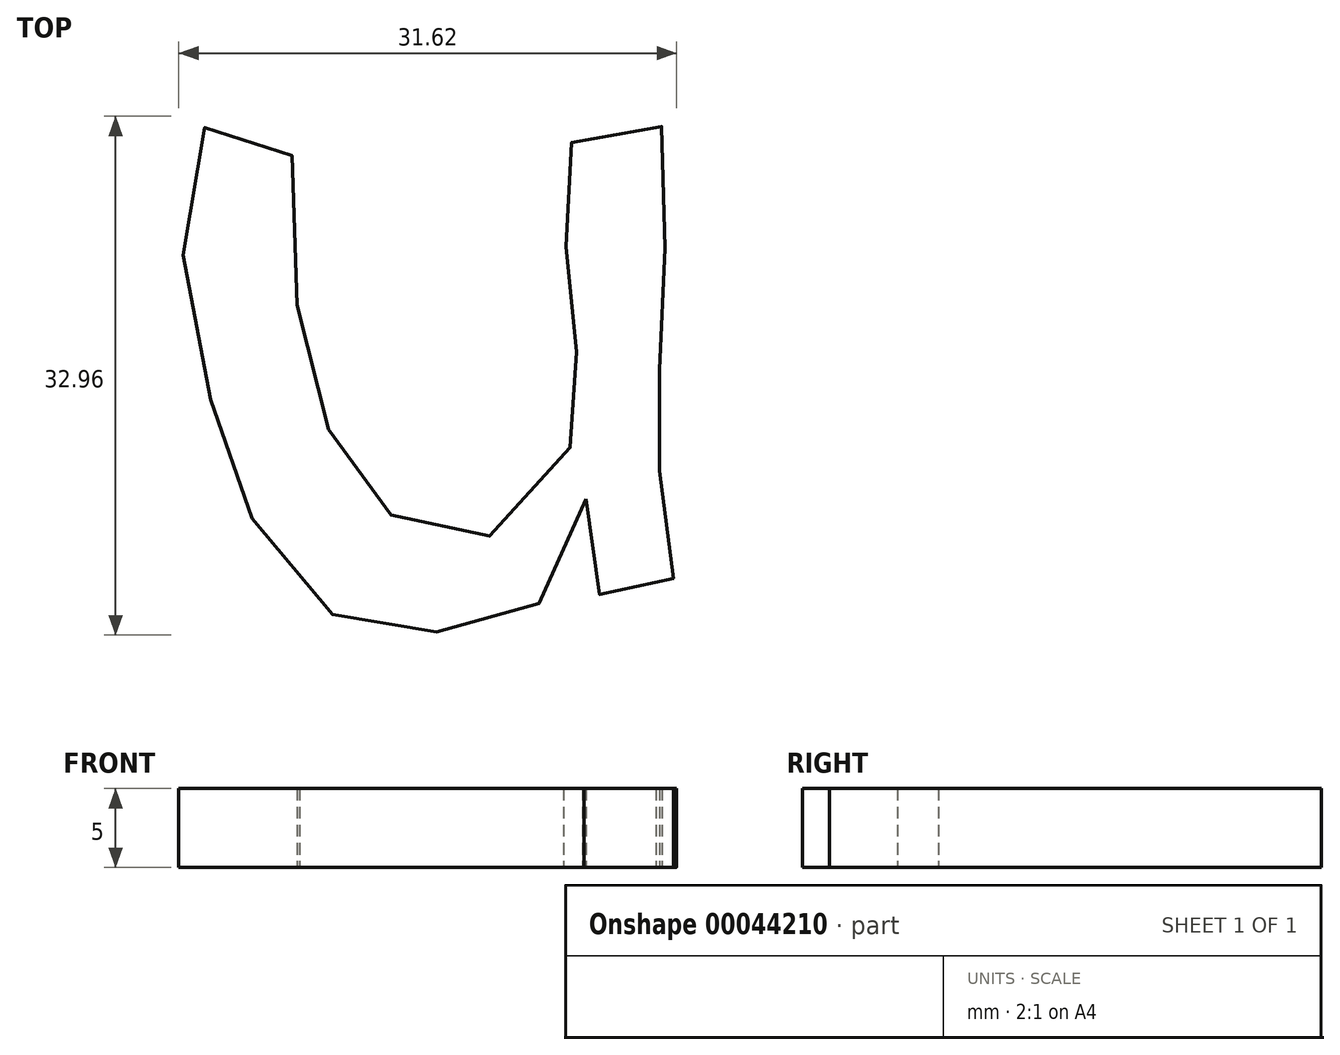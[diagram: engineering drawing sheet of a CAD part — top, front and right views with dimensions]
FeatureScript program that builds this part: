
annotation { "Feature Type Name" : "Feature", "Feature Type Description" : "" }
export const myFeature = defineFeature(function(context is Context, id is Id, definition is map)
    precondition{}
    {
        {
            var Q0;
            Q0=qCreatedBy(makeId("Top.planeOp"),FACE);
            var sketch = newSketch(context, id + "F0", { "sketchPlane" : qUnion([Q0])});
            skFitSpline(sketch, "E0", {"points": [v(-31.74, 13.31) * mm, v(-31.2, 7.66) * mm, v(-26.63, 7.13) * mm, v(-26.9, 12.77) * mm, v(-26.9, 19.5) * mm, v(-27.16, 26.5) * mm, v(-26.63, 36.71) * mm, v(-32, 36.71) * mm, v(-33.08, 31.33) * mm, v(-32.54, 23.8) * mm, v(-32, 19.23) * mm, v(-36.3, 11.7) * mm, v(-42.76, 11.43) * mm, v(-47.06, 16) * mm, v(-50.02, 24.34) * mm, v(-51.1, 36.44) * mm, v(-56.48, 36.44) * mm, v(-56.48, 24.07) * mm, v(-54.06, 14.66) * mm, v(-48.4, 6.32) * mm, v(-41.95, 4.98) * mm, v(-35.23, 6.05) * mm, v(-31.74, 13.31) * mm]});
            skSolve(sketch);
        }
        {
            var Q0;
            Q0=makeQuery(id+"F0.imprint","IMPRINT",FACE,{"disambiguationData":[TD([[makeQuery(id+"F0.imprint","IMPRINT",EDGE,{"derivedFrom":sQuery(id+"F0.wireOp",EDGE,"E0")}),1.0]])]});
            extrude(context, id + "F1", {"entities" : qUnion([Q0]), "depth" : 5 * mm});
        }
    });
